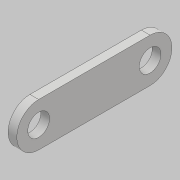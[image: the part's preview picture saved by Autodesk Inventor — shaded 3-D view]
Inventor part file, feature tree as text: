
AUTODESK INVENTOR PART (.ipt)
format: ipt  version: 2018 (Build 220112000, 112)  size: 87,552 bytes
history: native  units: mm
features: other x1, extrude x1, sketch x1
ambient origin geometry x8: Origin, YZ Plane, XZ Plane, XY Plane, X Axis, Y Axis, Z Axis, Center Point
bodies: Body1 (feature_tree)
feature tree (3):
  other  "實體1"
  extrude  "擠出1"  Depth=127.5mm
  sketch  "草圖1"
